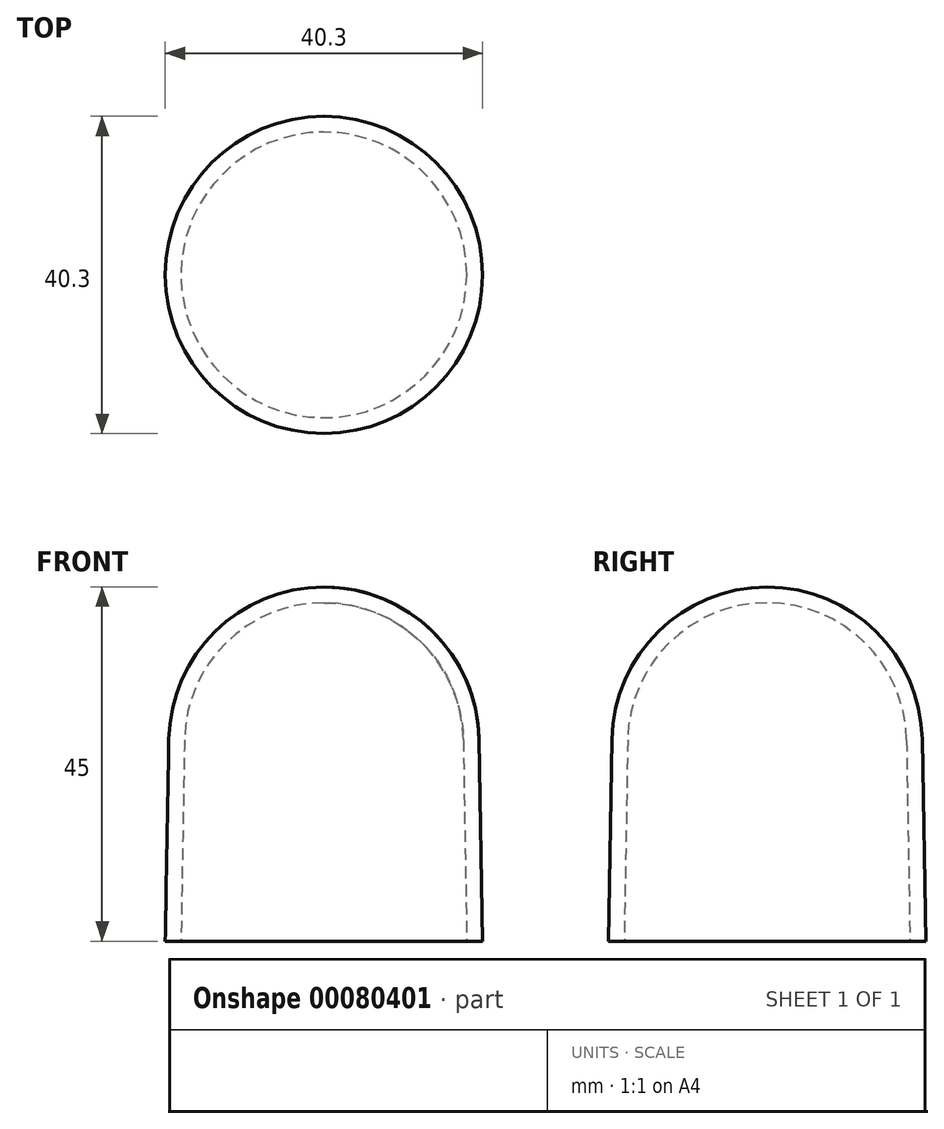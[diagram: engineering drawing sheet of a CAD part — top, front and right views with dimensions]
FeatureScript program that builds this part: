
annotation { "Feature Type Name" : "Feature", "Feature Type Description" : "" }
export const myFeature = defineFeature(function(context is Context, id is Id, definition is map)
    precondition{}
    {
        {
            var Q0;
            Q0=qCreatedBy(makeId("Front.planeOp"),FACE);
            var sketch = newSketch(context, id + "F0", { "sketchPlane" : qUnion([Q0])});
            skLineSegment(sketch, "E0", {"start": v(0, 0) * mm, "end": v(0, 45) * mm});
            skLineSegment(sketch, "E1", {"start": v(0, 0) * mm, "end": v(20.15, 0) * mm});
            skArc(sketch, "E2", {"start": v(0, 45) * mm, "mid": v(13.81, 39.35) * mm, "end": v(19.7, 25.64) * mm});
            skLineSegment(sketch, "E3", {"start": v(19.7, 25.64) * mm, "end": v(20.15, 0) * mm});
            skSolve(sketch);
        }
        {
            var Q0;
            Q0 = qSketchRegion(id + "F0", true);
            var Q1;
            Q1=sQuery(id+"F0.wireOp",EDGE,"E0");
            revolve(context, id + "F1", {"entities" : qUnion([Q0]), "axis" : qUnion([Q1]), "revolveType" : RevolveType.FULL});
        }
        {
            var Q0;
            Q0=makeQuery(id+"F1.opRevolve","SWEPT_FACE",FACE,{"disambiguationData":[OSD([sQuery(id+"F0.wireOp",EDGE,"E1")])]});
            shell(context, id + "F2", {"entities" : qUnion([Q0]), "thickness" : 2 * mm});
        }
    });
